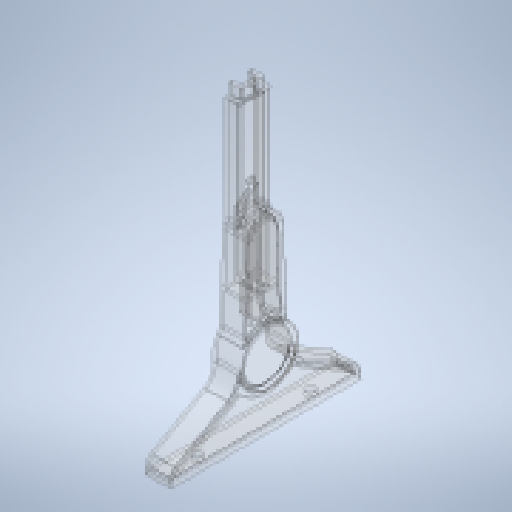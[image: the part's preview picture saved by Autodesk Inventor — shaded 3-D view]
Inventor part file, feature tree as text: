
AUTODESK INVENTOR PART (.ipt)
format: ipt  version: 2025.1 (Build 291241020, 241B)  size: 576,000 bytes
history: native  units: in
note: dims shown in document units (in); Inventor stores cm internally (conversion verified against a paired STEP export)
features: hole x1, sketch x1, other x1
ambient origin geometry x8: Origin, YZ Plane, XZ Plane, XY Plane, X Axis, Y Axis, Z Axis, Center Point
bodies: Solid1 (feature_tree)
feature tree (3):
  hole  "Hole1"  [1 undecoded]
  sketch  "Sketch1"  dims[d0=2.3622in d1=0.537in d2=4.0in d3=0.2685in d5=0.1969in d6=0.2362in d7=0.1575in d8=0.0787in d9=90.0deg d10=0.315in d11=0.8108in d12=2.3622in d13=0.2685in]
  other  "LEG"
note: 1 required parameter value undecoded (feature->parameter linkage not recoverable at this tier; creation-order binding heuristic only, values carry confidence <= 0.55)
